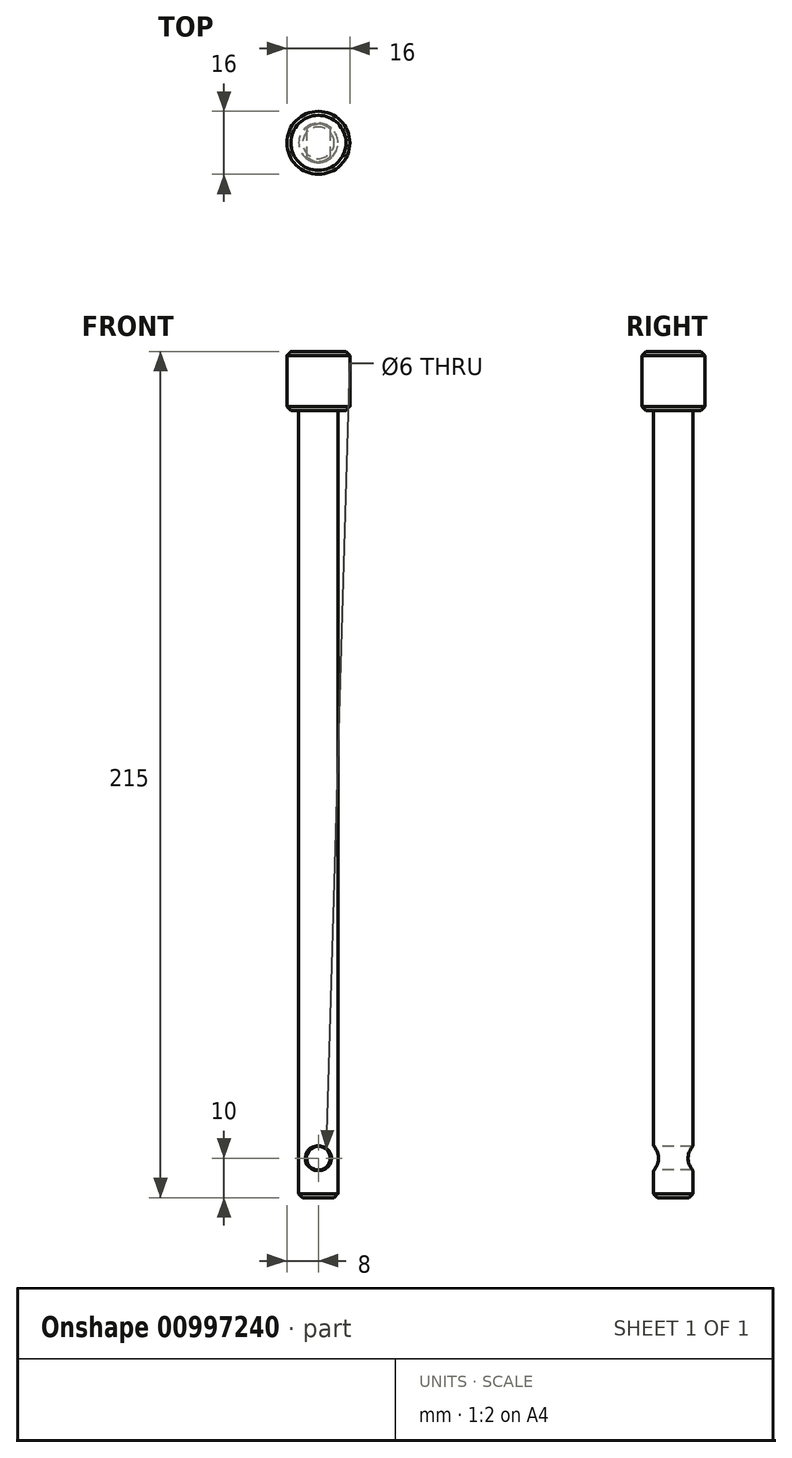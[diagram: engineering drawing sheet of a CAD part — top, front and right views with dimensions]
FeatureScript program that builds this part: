
annotation { "Feature Type Name" : "Feature", "Feature Type Description" : "" }
export const myFeature = defineFeature(function(context is Context, id is Id, definition is map)
    precondition{}
    {
        {
            var Q0;
            Q0=qCreatedBy(makeId("Front.planeOp"),FACE);
            var sketch = newSketch(context, id + "F0", { "sketchPlane" : qUnion([Q0])});
            skLineSegment(sketch, "E0", {"start": v(0, 17.67) * mm, "end": v(0, -20.08) * mm, "construction": true});
            skLineSegment(sketch, "E1", {"start": v(0, 107.5) * mm, "end": v(-8, 107.5) * mm});
            skLineSegment(sketch, "E2", {"start": v(-8, 107.5) * mm, "end": v(-8, 92.5) * mm});
            skLineSegment(sketch, "E3", {"start": v(-8, 92.5) * mm, "end": v(-5, 92.5) * mm});
            skLineSegment(sketch, "E4", {"start": v(-5, 92.5) * mm, "end": v(-5, -107.5) * mm});
            skLineSegment(sketch, "E5", {"start": v(-5, -107.5) * mm, "end": v(0, -107.5) * mm});
            skLineSegment(sketch, "E6", {"start": v(0, -107.5) * mm, "end": v(0, 107.5) * mm});
            skSolve(sketch);
        }
        {
            var Q0;
            Q0 = qSketchRegion(id + "F0", true);
            var Q1;
            Q1=sQuery(id+"F0.wireOp",EDGE,"E6");
            revolve(context, id + "F1", {"surfaceOperationType" : NewSurfaceOperationType.NEW, "entities" : qUnion([Q0]), "axis" : qUnion([Q1]), "revolveType" : RevolveType.FULL});
        }
        {
            var Q0;
            Q0=makeQuery(id+"F1.opRevolve","SWEPT_EDGE",EDGE,{"disambiguationData":[OSD([sQuery(id+"F0.wireOp",EDGE,"E1"),sQuery(id+"F0.wireOp",EDGE,"E2")])]});
            var Q1;
            Q1=makeQuery(id+"F1.opRevolve","SWEPT_EDGE",EDGE,{"disambiguationData":[OSD([sQuery(id+"F0.wireOp",EDGE,"E2"),sQuery(id+"F0.wireOp",EDGE,"E3")])]});
            var Q2;
            Q2=makeQuery(id+"F1.opRevolve","SWEPT_EDGE",EDGE,{"disambiguationData":[OSD([sQuery(id+"F0.wireOp",EDGE,"E4"),sQuery(id+"F0.wireOp",EDGE,"E5")])]});
            chamfer(context, id + "F2", {"entities" : qUnion([Q0, Q1, Q2]), "width" : 1 * mm, "tangentPropagation" : true});
        }
        {
            var Q0;
            Q0=makeQuery(id+"F1.opRevolve","SWEPT_EDGE",EDGE,{"disambiguationData":[OSD([sQuery(id+"F0.wireOp",EDGE,"E3"),sQuery(id+"F0.wireOp",EDGE,"E4")])]});
            fillet(context, id + "F3", {"entities" : qUnion([Q0]), "radius" : 0.2 * mm, "tangentPropagation" : true, "allowEdgeOverflow" : false});
        }
        {
            var Q0;
            Q0=qCreatedBy(makeId("Front.planeOp"),FACE);
            var sketch = newSketch(context, id + "F4", { "sketchPlane" : qUnion([Q0])});
            skCircle(sketch, "E7", {"center": v(0, -97.5) * mm, "radius": 3 * mm});
            skSolve(sketch);
        }
        {
            var Q0;
            Q0 = qSketchRegion(id + "F4", true);
            extrude(context, id + "F5", {"entities" : qUnion([Q0]), "operationType" : NewBodyOperationType.REMOVE, "endBound" : BoundingType.SYMMETRIC, "oppositeDirection" : true, "depth" : 25 * mm, "offsetDistance" : 25 * mm});
        }
        {
            var Q0;
            Q0=makeQuery(id+"F5.boolean.opBoolean","INTERSECT",EDGE,{"disambiguationData":[OD(0.0)],"derivedFrom":[makeQuery(id+"F1.opRevolve","SWEPT_FACE",FACE,{"disambiguationData":[OSD([sQuery(id+"F0.wireOp",EDGE,"E4")])]}),makeQuery(id+"F5.opExtrude","SWEPT_FACE",FACE,{"disambiguationData":[OSD([sQuery(id+"F4.wireOp",EDGE,"E7")])]})]});
            var Q1;
            Q1=makeQuery(id+"F5.boolean.opBoolean","INTERSECT",EDGE,{"disambiguationData":[OD(1.0)],"derivedFrom":[makeQuery(id+"F1.opRevolve","SWEPT_FACE",FACE,{"disambiguationData":[OSD([sQuery(id+"F0.wireOp",EDGE,"E4")])]}),makeQuery(id+"F5.opExtrude","SWEPT_FACE",FACE,{"disambiguationData":[OSD([sQuery(id+"F4.wireOp",EDGE,"E7")])]})]});
            chamfer(context, id + "F6", {"entities" : qUnion([Q0, Q1]), "width" : 0.2 * mm, "tangentPropagation" : true});
        }
    });
